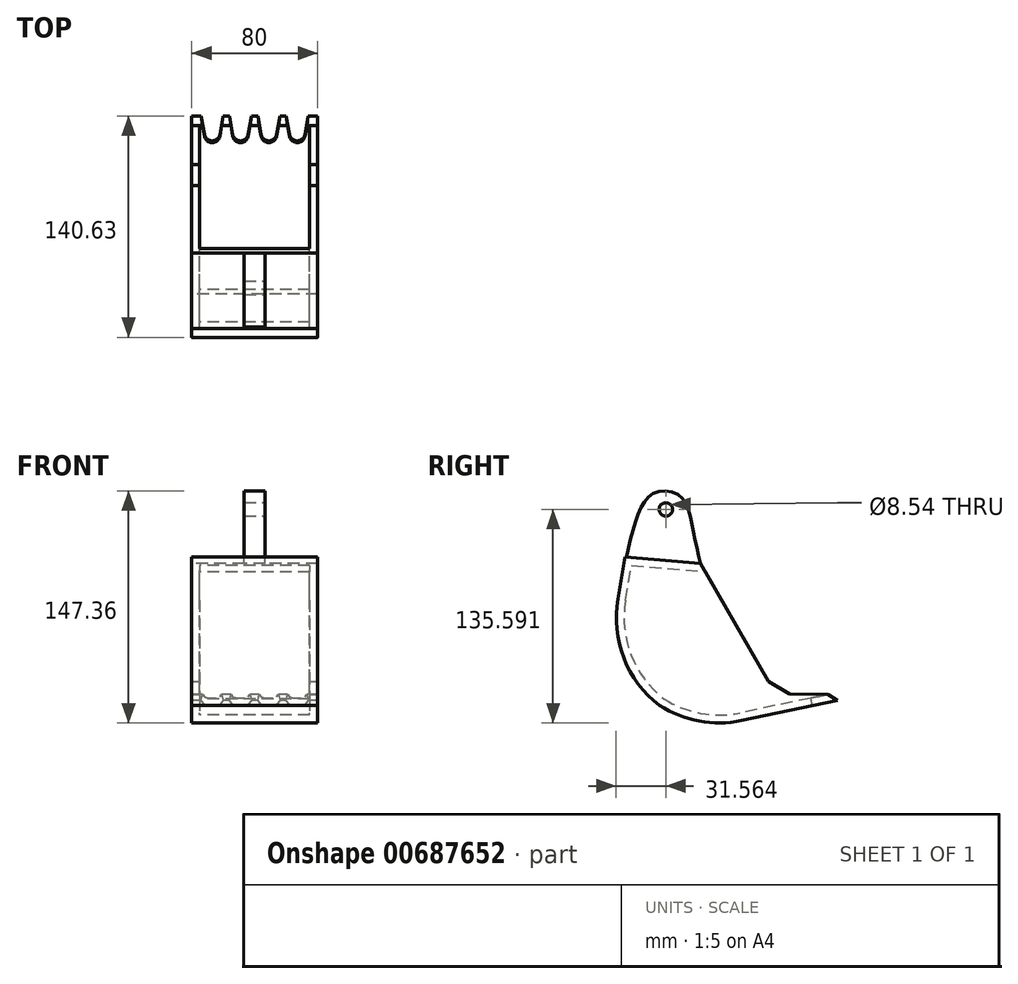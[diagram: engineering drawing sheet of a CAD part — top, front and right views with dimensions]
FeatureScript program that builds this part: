
annotation { "Feature Type Name" : "Feature", "Feature Type Description" : "" }
export const myFeature = defineFeature(function(context is Context, id is Id, definition is map)
    precondition{}
    {
        {
            var Q0;
            Q0=qCreatedBy(makeId("Right.planeOp"),FACE);
            var sketch = newSketch(context, id + "F0", { "sketchPlane" : qUnion([Q0])});
            skLineSegment(sketch, "E0", {"start": v(-81.75, 41.26) * mm, "end": v(-33.87, 37.18) * mm});
            skLineSegment(sketch, "E1", {"start": v(-33.87, 37.18) * mm, "end": v(15.03, -25.47) * mm});
            skLineSegment(sketch, "E2", {"start": v(15.03, -25.47) * mm, "end": v(53.23, -49.92) * mm});
            skLineSegment(sketch, "E3", {"start": v(53.23, -49.92) * mm, "end": v(-37.44, -68.76) * mm});
            skLineSegment(sketch, "E4", {"start": v(-37.44, -68.76) * mm, "end": v(-93.97, -29.03) * mm});
            skLineSegment(sketch, "E5", {"start": v(-93.97, -29.03) * mm, "end": v(-81.75, 41.26) * mm});
            skSolve(sketch);
        }
        {
            var Q0;
            Q0=makeQuery(id+"F0.imprint","IMPRINT",FACE,{"disambiguationData":[TD([[makeQuery(id+"F0.imprint","IMPRINT",EDGE,{"derivedFrom":sQuery(id+"F0.wireOp",EDGE,"E0")}),-1.0]])]});
            extrude(context, id + "F1", {"entities" : qUnion([Q0]), "depth" : 80 * mm, "offsetDistance" : 25 * mm});
        }
        {
            var Q0;
            Q0=makeQuery(id+"F1.opExtrude","SWEPT_EDGE",EDGE,{"disambiguationData":[OSD([sQuery(id+"F0.wireOp",EDGE,"E4"),sQuery(id+"F0.wireOp",EDGE,"E5")])]});
            var Q1;
            Q1=makeQuery(id+"F1.opExtrude","SWEPT_EDGE",EDGE,{"disambiguationData":[OSD([sQuery(id+"F0.wireOp",EDGE,"E3"),sQuery(id+"F0.wireOp",EDGE,"E4")])]});
            fillet(context, id + "F2", {"entities" : qUnion([Q0, Q1]), "radius" : 70 * mm, "tangentPropagation" : true, "allowEdgeOverflow" : false});
        }
        {
            var Q0;
            Q0=makeQuery(id+"F1.opExtrude","SWEPT_FACE",FACE,{"disambiguationData":[OSD([sQuery(id+"F0.wireOp",EDGE,"E1")])]});
            var Q1;
            Q1=makeQuery(id+"F1.opExtrude","SWEPT_FACE",FACE,{"disambiguationData":[OSD([sQuery(id+"F0.wireOp",EDGE,"E2")])]});
            shell(context, id + "F3", {"entities" : qUnion([Q0, Q1]), "thickness" : 5 * mm});
        }
        {
            var Q0;
            Q0=makeQuery(id+"F1.opExtrude","SWEPT_FACE",FACE,{"disambiguationData":[OSD([sQuery(id+"F0.wireOp",EDGE,"E0")])]});
            var sketch = newSketch(context, id + "F4", { "sketchPlane" : qUnion([Q0])});
            skLineSegment(sketch, "E6.bottom", {"start": v(33.34, -36.9) * mm, "end": v(46.66, -36.9) * mm});
            skLineSegment(sketch, "E6.top", {"start": v(33.34, -84.04) * mm, "end": v(46.66, -84.04) * mm});
            skLineSegment(sketch, "E6.left", {"start": v(33.34, -36.9) * mm, "end": v(33.34, -84.04) * mm});
            skLineSegment(sketch, "E6.right", {"start": v(46.66, -36.9) * mm, "end": v(46.66, -84.04) * mm});
            skPoint(sketch, "E6.middle", {"position": v(40, -60.47) * mm});
            skPoint(sketch, "E6.middle.positionSnap0", {"position": v(40, -84.95) * mm});
            skPoint(sketch, "E6.centerSnap0", {"position": v(40, -84.95) * mm});
            skSolve(sketch);
        }
        {
            var Q0;
            Q0=makeQuery(id+"F4.imprint","IMPRINT",FACE,{"disambiguationData":[TD([[makeQuery(id+"F4.imprint","IMPRINT",EDGE,{"derivedFrom":sQuery(id+"F4.wireOp",EDGE,"E6.bottom")}),1.0]])]});
            extrude(context, id + "F5", {"entities" : qUnion([Q0]), "operationType" : NewBodyOperationType.ADD, "depth" : 46.5 * mm, "offsetDistance" : 25 * mm});
        }
        {
            var Q0;
            Q0=makeQuery(id+"F5.opExtrude","SWEPT_FACE",FACE,{"disambiguationData":[OSD([sQuery(id+"F4.wireOp",EDGE,"E6.right")])]});
            var sketch = newSketch(context, id + "F6", { "sketchPlane" : qUnion([Q0])});
            skFitSpline(sketch, "E7", {"points": [v(-80.84, 41.18) * mm, v(-72.4, 71) * mm, v(-61.96, 82.52) * mm, v(-46.47, 79.81) * mm, v(-39.45, 62.7) * mm, v(-33.87, 37.18) * mm], "startDerivative": vector(30.09, 134.5) * mm, "endDerivative": vector(26.07, -116.46) * mm});
            skCircle(sketch, "E8", {"center": v(-55.84, 71.53) * mm, "radius": 4.27 * mm});
            skLineSegment(sketch, "E9", {"start": v(-80.84, 41.18) * mm, "end": v(-33.87, 37.18) * mm});
            skSolve(sketch);
        }
        {
            var Q0;
            Q0=makeQuery(id+"F6.imprint","IMPRINT",FACE,{"disambiguationData":[TD([[makeQuery(id+"F6.imprint","IMPRINT",EDGE,{"derivedFrom":sQuery(id+"F6.wireOp",EDGE,"E7")}),1.0]])]});
            var Q1;
            Q1=makeQuery(id+"F6.imprint","IMPRINT",FACE,{"disambiguationData":[TD([[makeQuery(id+"F6.imprint","IMPRINT",EDGE,{"derivedFrom":sQuery(id+"F6.wireOp",EDGE,"E8")}),1.0]])]});
            extrude(context, id + "F7", {"entities" : qUnion([Q0, Q1]), "operationType" : NewBodyOperationType.REMOVE, "oppositeDirection" : true, "depth" : 25 * mm, "offsetDistance" : 25 * mm});
        }
        {
            var Q0;
            Q0=makeQuery(id+"F1.opExtrude","CAP_FACE",FACE,{"disambiguationData":[OSD([sQuery(id+"F0.wireOp",EDGE,"E0"),sQuery(id+"F0.wireOp",EDGE,"E1"),sQuery(id+"F0.wireOp",EDGE,"E2"),sQuery(id+"F0.wireOp",EDGE,"E3"),sQuery(id+"F0.wireOp",EDGE,"E4"),sQuery(id+"F0.wireOp",EDGE,"E5")])],"isStart":false});
            var sketch = newSketch(context, id + "F8", { "sketchPlane" : qUnion([Q0])});
            skLineSegment(sketch, "E10", {"start": v(47.2, -46.06) * mm, "end": v(22.49, -45.6) * mm});
            skLineSegment(sketch, "E11", {"start": v(22.49, -45.6) * mm, "end": v(9.2, -37.67) * mm});
            skLineSegment(sketch, "E12", {"start": v(9.2, -37.67) * mm, "end": v(-33.87, 37.18) * mm});
            skSolve(sketch);
        }
        {
            var Q0;
            {var subQ1=sQuery(id+"F8.wireOp",EDGE,"E10");Q0=makeQuery(id+"F8.imprint","IMPRINT",FACE,{"disambiguationData":[TD([[makeQuery(id+"F8.imprint","IMPRINT",EDGE,{"derivedFrom":subQ1}),-1.0]])]});}
            extrude(context, id + "F9", {"entities" : qUnion([Q0]), "operationType" : NewBodyOperationType.REMOVE, "oppositeDirection" : true, "depth" : 146.3 * mm, "offsetDistance" : 25 * mm});
        }
        {
            var Q0;
            Q0=makeQuery(id+"F3.opShell","OFFSET_FACE",FACE,{"disambiguationData":[OSD([sQuery(id+"F0.wireOp",EDGE,"E3")])]});
            var sketch = newSketch(context, id + "F10", { "sketchPlane" : qUnion([Q0])});
            skLineSegment(sketch, "E13", {"start": v(5, 48.06) * mm, "end": v(8.08, 29.97) * mm});
            skLineSegment(sketch, "E14", {"start": v(17.93, 29.97) * mm, "end": v(21.01, 48.06) * mm});
            skLineSegment(sketch, "E15", {"start": v(21.01, 48.06) * mm, "end": v(5, 48.06) * mm});
            skPoint(sketch, "E16.visualSharp", {"position": v(13, 0.96) * mm});
            skArc(sketch, "E16.filletArc", {"start": v(8.08, 29.97) * mm, "mid": v(13, 25.8) * mm, "end": v(17.93, 29.97) * mm});
            skPoint(sketch, "E17", {"position": v(13, 48.06) * mm});
            skLineSegment(sketch, "E18.1.0.0", {"start": v(23, 48.06) * mm, "end": v(26.07, 29.97) * mm});
            skArc(sketch, "E18.1.0.1", {"start": v(26.07, 29.97) * mm, "mid": v(31, 25.8) * mm, "end": v(35.93, 29.97) * mm});
            skLineSegment(sketch, "E18.1.0.2", {"start": v(35.93, 29.97) * mm, "end": v(39, 48.06) * mm});
            skLineSegment(sketch, "E18.1.0.3", {"start": v(39, 48.06) * mm, "end": v(23, 48.06) * mm});
            skLineSegment(sketch, "E18.2.0.0", {"start": v(41, 48.06) * mm, "end": v(44.07, 29.97) * mm});
            skArc(sketch, "E18.2.0.1", {"start": v(44.07, 29.97) * mm, "mid": v(49, 25.8) * mm, "end": v(53.93, 29.97) * mm});
            skLineSegment(sketch, "E18.2.0.2", {"start": v(53.93, 29.97) * mm, "end": v(57, 48.06) * mm});
            skLineSegment(sketch, "E18.2.0.3", {"start": v(57, 48.06) * mm, "end": v(41, 48.06) * mm});
            skLineSegment(sketch, "E18.3.0.0", {"start": v(58.99, 48.06) * mm, "end": v(62.07, 29.97) * mm});
            skArc(sketch, "E18.3.0.1", {"start": v(62.07, 29.97) * mm, "mid": v(67, 25.8) * mm, "end": v(71.92, 29.97) * mm});
            skLineSegment(sketch, "E18.3.0.2", {"start": v(71.92, 29.97) * mm, "end": v(75, 48.06) * mm});
            skLineSegment(sketch, "E18.3.0.3", {"start": v(75, 48.06) * mm, "end": v(58.99, 48.06) * mm});
            skLineSegment(sketch, "E18.direction1", {"start": v(8.08, 29.97) * mm, "end": v(26.07, 29.97) * mm, "construction": true});
            skSolve(sketch);
        }
        {
            var Q0;
            {var subQ1=sQuery(id+"F10.wireOp",EDGE,"E13");Q0=makeQuery(id+"F10.imprint","IMPRINT",FACE,{"disambiguationData":[TD([[makeQuery(id+"F10.imprint","IMPRINT",EDGE,{"derivedFrom":subQ1}),1.0]])]});}
            var Q1;
            {var subQ0=sQuery(id+"F10.wireOp",EDGE,"E16.filletArc");var subQ1=makeQuery(id+"F3.opShell","OFFSET_EDGE",EDGE,{"disambiguationData":[OSD([sQuery(id+"F0.wireOp",EDGE,"E2"),sQuery(id+"F0.wireOp",EDGE,"E3")])]});var subQ2=makeQuery(id+"F10.imprint","INTERSECT",VERTEX,{"disambiguationData":[OD(0.0)],"derivedFrom":[subQ1,subQ0]});Q1=makeQuery(id+"F10.imprint","IMPRINT",FACE,{"disambiguationData":[TD([[makeQuery(id+"F10.imprint","IMPRINT",EDGE,{"disambiguationData":[TD([[subQ2,-1.0]])],"derivedFrom":subQ0}),1.0]])]});}
            var Q2;
            {var subQ0=sQuery(id+"F10.wireOp",EDGE,"E18.1.0.1");var subQ1=makeQuery(id+"F3.opShell","OFFSET_EDGE",EDGE,{"disambiguationData":[OSD([sQuery(id+"F0.wireOp",EDGE,"E2"),sQuery(id+"F0.wireOp",EDGE,"E3")])]});var subQ2=makeQuery(id+"F10.imprint","INTERSECT",VERTEX,{"disambiguationData":[OD(0.0)],"derivedFrom":[subQ1,subQ0]});Q2=makeQuery(id+"F10.imprint","IMPRINT",FACE,{"disambiguationData":[TD([[makeQuery(id+"F10.imprint","IMPRINT",EDGE,{"disambiguationData":[TD([[subQ2,-1.0]])],"derivedFrom":subQ0}),1.0]])]});}
            var Q3;
            {var subQ4=sQuery(id+"F10.wireOp",EDGE,"E18.1.0.0");Q3=makeQuery(id+"F10.imprint","IMPRINT",FACE,{"disambiguationData":[TD([[makeQuery(id+"F10.imprint","IMPRINT",EDGE,{"derivedFrom":subQ4}),1.0]])]});}
            var Q4;
            {var subQ0=sQuery(id+"F10.wireOp",EDGE,"E18.2.0.1");var subQ1=makeQuery(id+"F3.opShell","OFFSET_EDGE",EDGE,{"disambiguationData":[OSD([sQuery(id+"F0.wireOp",EDGE,"E2"),sQuery(id+"F0.wireOp",EDGE,"E3")])]});var subQ2=makeQuery(id+"F10.imprint","INTERSECT",VERTEX,{"disambiguationData":[OD(0.0)],"derivedFrom":[subQ1,subQ0]});Q4=makeQuery(id+"F10.imprint","IMPRINT",FACE,{"disambiguationData":[TD([[makeQuery(id+"F10.imprint","IMPRINT",EDGE,{"disambiguationData":[TD([[subQ2,-1.0]])],"derivedFrom":subQ0}),1.0]])]});}
            var Q5;
            {var subQ4=sQuery(id+"F10.wireOp",EDGE,"E18.2.0.0");Q5=makeQuery(id+"F10.imprint","IMPRINT",FACE,{"disambiguationData":[TD([[makeQuery(id+"F10.imprint","IMPRINT",EDGE,{"derivedFrom":subQ4}),1.0]])]});}
            var Q6;
            {var subQ0=sQuery(id+"F10.wireOp",EDGE,"E18.3.0.1");var subQ1=makeQuery(id+"F3.opShell","OFFSET_EDGE",EDGE,{"disambiguationData":[OSD([sQuery(id+"F0.wireOp",EDGE,"E2"),sQuery(id+"F0.wireOp",EDGE,"E3")])]});var subQ2=makeQuery(id+"F10.imprint","INTERSECT",VERTEX,{"disambiguationData":[OD(0.0)],"derivedFrom":[subQ1,subQ0]});Q6=makeQuery(id+"F10.imprint","IMPRINT",FACE,{"disambiguationData":[TD([[makeQuery(id+"F10.imprint","IMPRINT",EDGE,{"disambiguationData":[TD([[subQ2,-1.0]])],"derivedFrom":subQ0}),1.0]])]});}
            var Q7;
            {var subQ4=sQuery(id+"F10.wireOp",EDGE,"E18.3.0.0");Q7=makeQuery(id+"F10.imprint","IMPRINT",FACE,{"disambiguationData":[TD([[makeQuery(id+"F10.imprint","IMPRINT",EDGE,{"derivedFrom":subQ4}),1.0]])]});}
            extrude(context, id + "F11", {"entities" : qUnion([Q0, Q1, Q2, Q3, Q4, Q5, Q6, Q7]), "operationType" : NewBodyOperationType.REMOVE, "oppositeDirection" : true, "depth" : 25 * mm, "offsetDistance" : 25 * mm});
        }
    });
